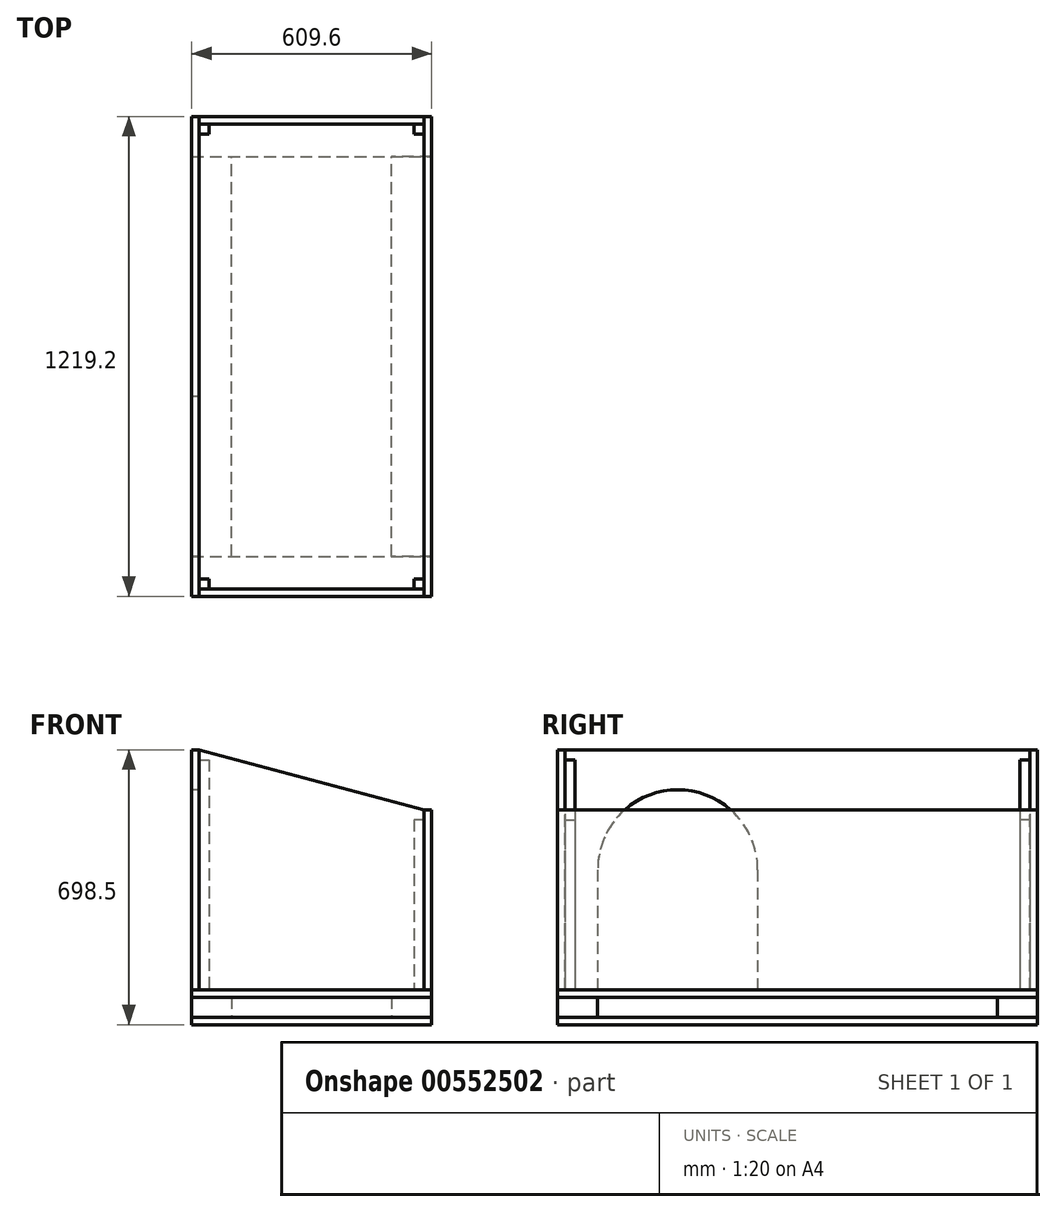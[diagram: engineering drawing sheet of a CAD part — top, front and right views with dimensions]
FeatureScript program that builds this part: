
annotation { "Feature Type Name" : "Feature", "Feature Type Description" : "" }
export const myFeature = defineFeature(function(context is Context, id is Id, definition is map)
    precondition{}
    {
        {
            var Q0;
            Q0=qCreatedBy(makeId("Top.planeOp"),FACE);
            var sketch = newSketch(context, id + "F0", { "sketchPlane" : qUnion([Q0])});
            skLineSegment(sketch, "E0.bottom", {"start": v(307.44, 609.6) * mm, "end": v(-302.16, 609.6) * mm});
            skLineSegment(sketch, "E0.top", {"start": v(307.44, -609.6) * mm, "end": v(-302.16, -609.6) * mm});
            skLineSegment(sketch, "E0.left", {"start": v(307.44, 609.6) * mm, "end": v(307.44, -609.6) * mm});
            skLineSegment(sketch, "E0.right", {"start": v(-302.16, 609.6) * mm, "end": v(-302.16, -609.6) * mm});
            skPoint(sketch, "E0.middle", {"position": v(2.64, 0) * mm});
            skSolve(sketch);
        }
        {
            var Q0;
            Q0 = qSketchRegion(id + "F0", true);
            extrude(context, id + "F1", {"entities" : qUnion([Q0]), "oppositeDirection" : true, "depth" : 19.05 * mm, "offsetDistance" : 25.4 * mm});
        }
        {
            var Q0;
            Q0=makeQuery(id+"F1.opExtrude","CAP_FACE",FACE,{"disambiguationData":[OSD([sQuery(id+"F0.wireOp",EDGE,"E0.bottom"),sQuery(id+"F0.wireOp",EDGE,"E0.top"),sQuery(id+"F0.wireOp",EDGE,"E0.left"),sQuery(id+"F0.wireOp",EDGE,"E0.right")])],"isStart":true});
            var sketch = newSketch(context, id + "F2", { "sketchPlane" : qUnion([Q0])});
            skLineSegment(sketch, "E1.bottom", {"start": v(-302.16, -609.6) * mm, "end": v(307.44, -609.6) * mm});
            skLineSegment(sketch, "E1.top", {"start": v(-302.16, -508) * mm, "end": v(307.44, -508) * mm});
            skLineSegment(sketch, "E1.left", {"start": v(-302.16, -609.6) * mm, "end": v(-302.16, -508) * mm});
            skLineSegment(sketch, "E1.right", {"start": v(307.44, -609.6) * mm, "end": v(307.44, -508) * mm});
            skSolve(sketch);
        }
        {
            var Q0;
            Q0 = qSketchRegion(id + "F2", true);
            extrude(context, id + "F3", {"entities" : qUnion([Q0]), "depth" : 50.8 * mm, "offsetDistance" : 25.4 * mm});
        }
        {
            var Q0;
            Q0=makeQuery(id+"F3.opExtrude","SWEPT_BODY",BODY,{"disambiguationData":[OSD([sQuery(id+"F2.wireOp",EDGE,"E1.bottom"),sQuery(id+"F2.wireOp",EDGE,"E1.top"),sQuery(id+"F2.wireOp",EDGE,"E1.left"),sQuery(id+"F2.wireOp",EDGE,"E1.right")])]});
            var Q1;
            Q1=qCreatedBy(makeId("Front.planeOp"),FACE);
            mirror(context, id + "F4", {"entities" : qUnion([Q0]), "mirrorPlane" : qUnion([Q1])});
        }
        {
            var Q0;
            Q0=makeQuery(id+"F1.opExtrude","CAP_FACE",FACE,{"disambiguationData":[OSD([sQuery(id+"F0.wireOp",EDGE,"E0.bottom"),sQuery(id+"F0.wireOp",EDGE,"E0.top"),sQuery(id+"F0.wireOp",EDGE,"E0.left"),sQuery(id+"F0.wireOp",EDGE,"E0.right")])],"isStart":true});
            var sketch = newSketch(context, id + "F5", { "sketchPlane" : qUnion([Q0])});
            skPoint(sketch, "E2.0", {"position": v(307.44, -508) * mm});
            skPoint(sketch, "E3.0", {"position": v(307.44, 508) * mm});
            skLineSegment(sketch, "E4.0", {"start": v(-302.16, 508) * mm, "end": v(307.44, 508) * mm, "construction": true});
            skLineSegment(sketch, "E5.bottom", {"start": v(307.44, -508) * mm, "end": v(205.84, -508) * mm});
            skLineSegment(sketch, "E5.top", {"start": v(307.44, 508) * mm, "end": v(205.84, 508) * mm});
            skLineSegment(sketch, "E5.left", {"start": v(307.44, -508) * mm, "end": v(307.44, 508) * mm});
            skLineSegment(sketch, "E5.right", {"start": v(205.84, -508) * mm, "end": v(205.84, 508) * mm});
            skSolve(sketch);
        }
        {
            var Q0;
            Q0 = qSketchRegion(id + "F5", true);
            extrude(context, id + "F6", {"entities" : qUnion([Q0]), "depth" : 50.8 * mm, "offsetDistance" : 25.4 * mm});
        }
        {
            var Q0;
            Q0=makeQuery(id+"F1.opExtrude","CAP_FACE",FACE,{"disambiguationData":[OSD([sQuery(id+"F0.wireOp",EDGE,"E0.bottom"),sQuery(id+"F0.wireOp",EDGE,"E0.top"),sQuery(id+"F0.wireOp",EDGE,"E0.left"),sQuery(id+"F0.wireOp",EDGE,"E0.right")])],"isStart":true});
            var sketch = newSketch(context, id + "F7", { "sketchPlane" : qUnion([Q0])});
            skPoint(sketch, "E6.0", {"position": v(-302.16, -508) * mm});
            skLineSegment(sketch, "E7.0", {"start": v(-302.16, 508) * mm, "end": v(307.44, 508) * mm});
            skLineSegment(sketch, "E8.bottom", {"start": v(-302.16, -508) * mm, "end": v(-200.56, -508) * mm});
            skLineSegment(sketch, "E8.top", {"start": v(-302.16, 508) * mm, "end": v(-200.56, 508) * mm});
            skLineSegment(sketch, "E8.left", {"start": v(-302.16, -508) * mm, "end": v(-302.16, 508) * mm});
            skLineSegment(sketch, "E8.right", {"start": v(-200.56, -508) * mm, "end": v(-200.56, 508) * mm});
            skSolve(sketch);
        }
        {
            var Q0;
            Q0 = qSketchRegion(id + "F7", true);
            extrude(context, id + "F8", {"entities" : qUnion([Q0]), "depth" : 50.8 * mm, "offsetDistance" : 25.4 * mm});
        }
        {
            var Q0;
            Q0=makeQuery(id+"F4.opPattern","COPY",FACE,{"derivedFrom":makeQuery(id+"F3.opExtrude","CAP_FACE",FACE,{"disambiguationData":[OSD([sQuery(id+"F2.wireOp",EDGE,"E1.bottom"),sQuery(id+"F2.wireOp",EDGE,"E1.top"),sQuery(id+"F2.wireOp",EDGE,"E1.left"),sQuery(id+"F2.wireOp",EDGE,"E1.right")])],"isStart":false}),"instanceName":"1"});
            var sketch = newSketch(context, id + "F9", { "sketchPlane" : qUnion([Q0])});
            skPoint(sketch, "E9.0", {"position": v(-302.16, 609.6) * mm});
            skPoint(sketch, "E10.0", {"position": v(307.44, -609.6) * mm});
            skLineSegment(sketch, "E11.0", {"start": v(-302.16, 508) * mm, "end": v(-302.16, 609.6) * mm});
            skLineSegment(sketch, "E12.bottom", {"start": v(-302.16, 609.6) * mm, "end": v(307.44, 609.6) * mm});
            skLineSegment(sketch, "E12.top", {"start": v(-302.16, -609.6) * mm, "end": v(307.44, -609.6) * mm});
            skLineSegment(sketch, "E12.left", {"start": v(-302.16, 609.6) * mm, "end": v(-302.16, -609.6) * mm});
            skLineSegment(sketch, "E12.right", {"start": v(307.44, 609.6) * mm, "end": v(307.44, -609.6) * mm});
            skSolve(sketch);
        }
        {
            var Q0;
            Q0 = qSketchRegion(id + "F9", true);
            extrude(context, id + "F10", {"entities" : qUnion([Q0]), "depth" : 19.05 * mm, "offsetDistance" : 25.4 * mm});
        }
        {
            var Q0;
            Q0=makeQuery(id+"F10.opExtrude","SWEPT_FACE",FACE,{"disambiguationData":[OSD([sQuery(id+"F9.wireOp",EDGE,"E12.left")])]});
            var sketch = newSketch(context, id + "F11", { "sketchPlane" : qUnion([Q0])});
            skLineSegment(sketch, "E13.bottom", {"start": v(-609.6, 69.85) * mm, "end": v(609.6, 69.85) * mm});
            skLineSegment(sketch, "E13.top", {"start": v(-609.6, 679.45) * mm, "end": v(609.6, 679.45) * mm});
            skLineSegment(sketch, "E13.left", {"start": v(-609.6, 69.85) * mm, "end": v(-609.6, 679.45) * mm});
            skLineSegment(sketch, "E13.right", {"start": v(609.6, 69.85) * mm, "end": v(609.6, 679.45) * mm});
            skSolve(sketch);
        }
        {
            var Q0;
            Q0 = qSketchRegion(id + "F11", true);
            extrude(context, id + "F12", {"entities" : qUnion([Q0]), "oppositeDirection" : true, "depth" : 19.05 * mm, "offsetDistance" : 25.4 * mm});
        }
        {
            var Q0;
            Q0=makeQuery(id+"F10.opExtrude","SWEPT_FACE",FACE,{"disambiguationData":[OSD([sQuery(id+"F9.wireOp",EDGE,"E12.top")])]});
            var sketch = newSketch(context, id + "F13", { "sketchPlane" : qUnion([Q0])});
            skPoint(sketch, "E14.0", {"position": v(-283.11, 69.85) * mm});
            skLineSegment(sketch, "E15.bottom", {"start": v(-283.11, 69.85) * mm, "end": v(288.39, 69.85) * mm});
            skLineSegment(sketch, "E15.top", {"start": v(-283.11, 527.05) * mm, "end": v(288.39, 527.05) * mm});
            skLineSegment(sketch, "E15.left", {"start": v(-283.11, 69.85) * mm, "end": v(-283.11, 527.05) * mm});
            skLineSegment(sketch, "E15.right", {"start": v(288.39, 69.85) * mm, "end": v(288.39, 527.05) * mm});
            skPoint(sketch, "E16.0", {"position": v(-283.11, 679.45) * mm});
            skLineSegment(sketch, "E17", {"start": v(-283.11, 679.45) * mm, "end": v(288.39, 527.05) * mm});
            skLineSegment(sketch, "E18", {"start": v(-283.11, 527.05) * mm, "end": v(-283.11, 679.45) * mm});
            skSolve(sketch);
        }
        {
            var Q0;
            Q0 = qSketchRegion(id + "F13", true);
            extrude(context, id + "F14", {"entities" : qUnion([Q0]), "oppositeDirection" : true, "depth" : 19.05 * mm, "offsetDistance" : 25.4 * mm});
        }
        {
            var Q0;
            Q0=makeQuery(id+"F14.opExtrude","SWEPT_BODY",BODY,{"disambiguationData":[OSD([sQuery(id+"F13.wireOp",EDGE,"E15.bottom"),sQuery(id+"F13.wireOp",EDGE,"E15.top"),sQuery(id+"F13.wireOp",EDGE,"E15.left"),sQuery(id+"F13.wireOp",EDGE,"E15.right")])]});
            var Q1;
            Q1=qCreatedBy(makeId("Front.planeOp"),FACE);
            mirror(context, id + "F15", {"entities" : qUnion([Q0]), "mirrorPlane" : qUnion([Q1])});
        }
        {
            var Q0;
            Q0=makeQuery(id+"F6.opExtrude","SWEPT_FACE",FACE,{"disambiguationData":[OSD([sQuery(id+"F5.wireOp",EDGE,"E5.left")])]});
            var sketch = newSketch(context, id + "F16", { "sketchPlane" : qUnion([Q0])});
            skPoint(sketch, "E19.0", {"position": v(-609.6, 69.85) * mm});
            skPoint(sketch, "E20.0", {"position": v(609.6, 527.05) * mm});
            skLineSegment(sketch, "E21.bottom", {"start": v(-609.6, 69.85) * mm, "end": v(609.6, 69.85) * mm});
            skLineSegment(sketch, "E21.top", {"start": v(-609.6, 527.05) * mm, "end": v(609.6, 527.05) * mm});
            skLineSegment(sketch, "E21.left", {"start": v(-609.6, 69.85) * mm, "end": v(-609.6, 527.05) * mm});
            skLineSegment(sketch, "E21.right", {"start": v(609.6, 69.85) * mm, "end": v(609.6, 527.05) * mm});
            skSolve(sketch);
        }
        {
            var Q0;
            Q0 = qSketchRegion(id + "F16", true);
            extrude(context, id + "F17", {"entities" : qUnion([Q0]), "oppositeDirection" : true, "depth" : 19.05 * mm, "offsetDistance" : 25.4 * mm});
        }
        {
            var Q0;
            Q0=makeQuery(id+"F10.opExtrude","CAP_FACE",FACE,{"disambiguationData":[OSD([sQuery(id+"F9.wireOp",EDGE,"E12.bottom"),sQuery(id+"F9.wireOp",EDGE,"E12.top"),sQuery(id+"F9.wireOp",EDGE,"E12.left"),sQuery(id+"F9.wireOp",EDGE,"E12.right")])],"isStart":false});
            var sketch = newSketch(context, id + "F18", { "sketchPlane" : qUnion([Q0])});
            skPoint(sketch, "E22.0", {"position": v(-283.11, 590.55) * mm});
            skPoint(sketch, "E23.0", {"position": v(288.39, 590.55) * mm});
            skPoint(sketch, "E24.0", {"position": v(288.39, -590.55) * mm});
            skPoint(sketch, "E25.0", {"position": v(-283.11, -590.55) * mm});
            skLineSegment(sketch, "E26.bottom", {"start": v(-283.11, 590.55) * mm, "end": v(-257.71, 590.55) * mm});
            skLineSegment(sketch, "E26.top", {"start": v(-283.11, 565.15) * mm, "end": v(-257.71, 565.15) * mm});
            skLineSegment(sketch, "E26.left", {"start": v(-283.11, 590.55) * mm, "end": v(-283.11, 565.15) * mm});
            skLineSegment(sketch, "E26.right", {"start": v(-257.71, 590.55) * mm, "end": v(-257.71, 565.15) * mm});
            skLineSegment(sketch, "E27.bottom", {"start": v(-283.11, -590.55) * mm, "end": v(-257.71, -590.55) * mm});
            skLineSegment(sketch, "E27.top", {"start": v(-283.11, -565.15) * mm, "end": v(-257.71, -565.15) * mm});
            skLineSegment(sketch, "E27.left", {"start": v(-283.11, -590.55) * mm, "end": v(-283.11, -565.15) * mm});
            skLineSegment(sketch, "E27.right", {"start": v(-257.71, -590.55) * mm, "end": v(-257.71, -565.15) * mm});
            skSolve(sketch);
        }
        {
            var Q0;
            Q0 = qSketchRegion(id + "F18", true);
            extrude(context, id + "F19", {"entities" : qUnion([Q0]), "depth" : 584.2 * mm, "offsetDistance" : 25.4 * mm});
        }
        {
            var Q0;
            Q0=makeQuery(id+"F10.opExtrude","CAP_FACE",FACE,{"disambiguationData":[OSD([sQuery(id+"F9.wireOp",EDGE,"E12.bottom"),sQuery(id+"F9.wireOp",EDGE,"E12.top"),sQuery(id+"F9.wireOp",EDGE,"E12.left"),sQuery(id+"F9.wireOp",EDGE,"E12.right")])],"isStart":false});
            var sketch = newSketch(context, id + "F20", { "sketchPlane" : qUnion([Q0])});
            skPoint(sketch, "E28.0", {"position": v(288.39, 590.55) * mm});
            skPoint(sketch, "E29.0", {"position": v(288.39, -590.55) * mm});
            skLineSegment(sketch, "E30.bottom", {"start": v(288.39, 590.55) * mm, "end": v(262.99, 590.55) * mm});
            skLineSegment(sketch, "E30.top", {"start": v(288.39, 565.15) * mm, "end": v(262.99, 565.15) * mm});
            skLineSegment(sketch, "E30.left", {"start": v(288.39, 590.55) * mm, "end": v(288.39, 565.15) * mm});
            skLineSegment(sketch, "E30.right", {"start": v(262.99, 590.55) * mm, "end": v(262.99, 565.15) * mm});
            skLineSegment(sketch, "E31.bottom", {"start": v(288.39, -590.55) * mm, "end": v(262.99, -590.55) * mm});
            skLineSegment(sketch, "E31.top", {"start": v(288.39, -565.15) * mm, "end": v(262.99, -565.15) * mm});
            skLineSegment(sketch, "E31.left", {"start": v(288.39, -590.55) * mm, "end": v(288.39, -565.15) * mm});
            skLineSegment(sketch, "E31.right", {"start": v(262.99, -590.55) * mm, "end": v(262.99, -565.15) * mm});
            skSolve(sketch);
        }
        {
            var Q0;
            Q0 = qSketchRegion(id + "F20", true);
            extrude(context, id + "F21", {"entities" : qUnion([Q0]), "depth" : 431.8 * mm, "offsetDistance" : 25.4 * mm});
        }
        {
            var Q0;
            Q0=makeQuery(id+"F12.opExtrude","CAP_FACE",FACE,{"disambiguationData":[OSD([sQuery(id+"F11.wireOp",EDGE,"E13.bottom"),sQuery(id+"F11.wireOp",EDGE,"E13.top"),sQuery(id+"F11.wireOp",EDGE,"E13.left"),sQuery(id+"F11.wireOp",EDGE,"E13.right")])],"isStart":true});
            var sketch = newSketch(context, id + "F22", { "sketchPlane" : qUnion([Q0])});
            skLineSegment(sketch, "E32", {"start": v(609.6, 69.85) * mm, "end": v(508, 69.85) * mm, "construction": true});
            skLineSegment(sketch, "E33.bottom", {"start": v(508, 69.85) * mm, "end": v(101.6, 69.85) * mm});
            skLineSegment(sketch, "E33.top", {"start": v(508, 374.65) * mm, "end": v(101.6, 374.65) * mm});
            skLineSegment(sketch, "E33.left", {"start": v(508, 69.85) * mm, "end": v(508, 374.65) * mm});
            skLineSegment(sketch, "E33.right", {"start": v(101.6, 69.85) * mm, "end": v(101.6, 374.65) * mm});
            skPoint(sketch, "E34", {"position": v(304.8, 374.65) * mm});
            skCircle(sketch, "E35", {"center": v(304.8, 374.65) * mm, "radius": 203.2 * mm});
            skSolve(sketch);
        }
        {
            var Q0;
            Q0 = qSketchRegion(id + "F22", true);
            extrude(context, id + "F23", {"entities" : qUnion([Q0]), "operationType" : NewBodyOperationType.REMOVE, "endBound" : BoundingType.UP_TO_NEXT, "oppositeDirection" : true, "depth" : 19.05 * mm, "offsetDistance" : 25.4 * mm});
        }
    });
